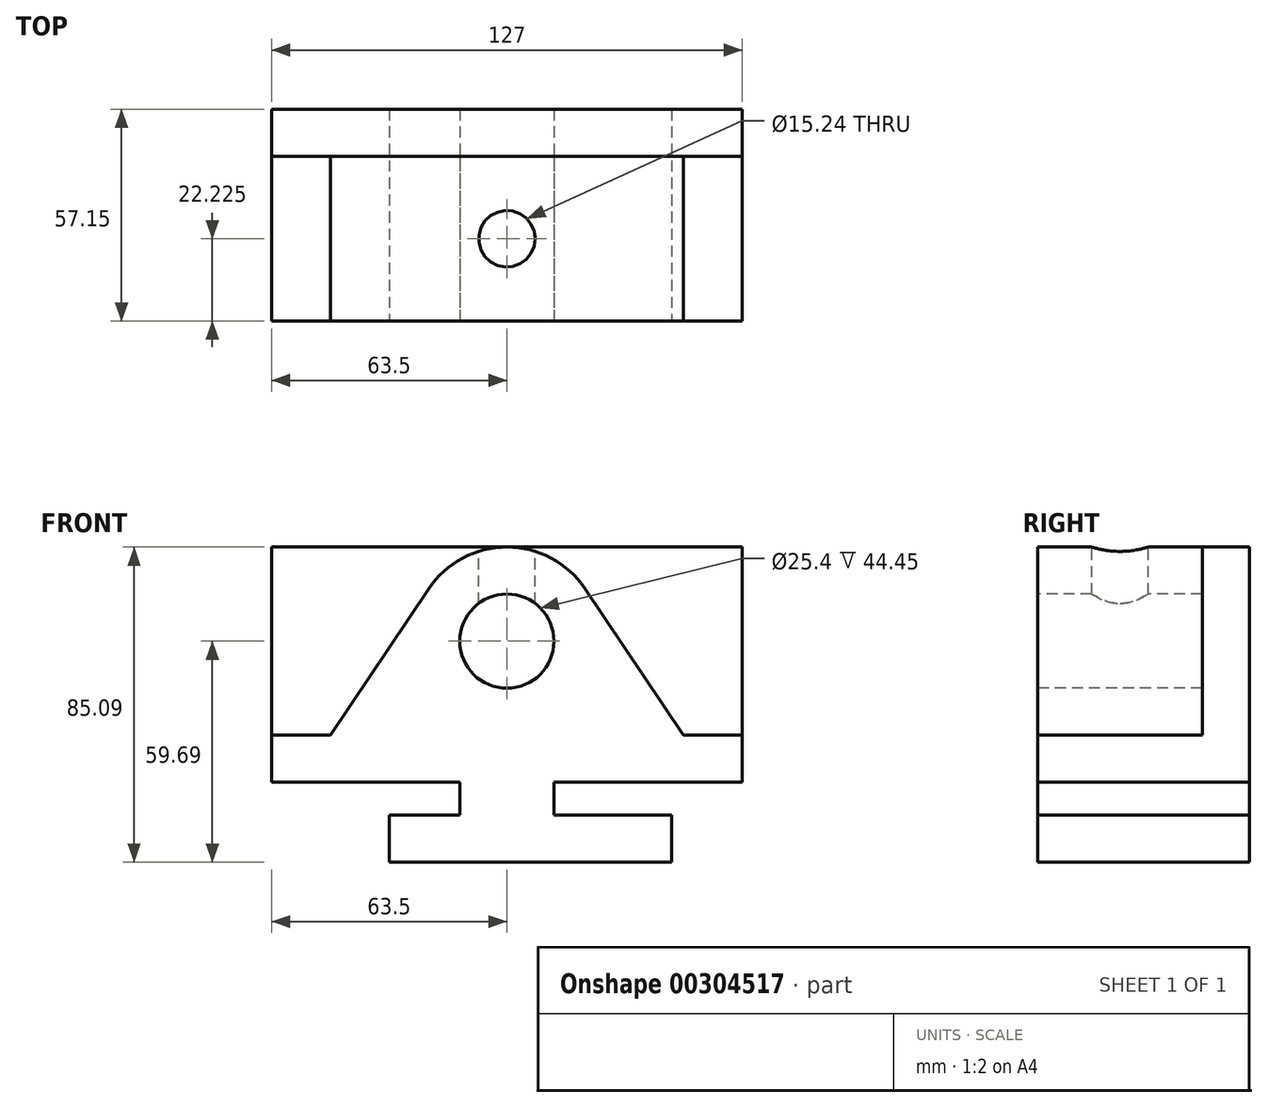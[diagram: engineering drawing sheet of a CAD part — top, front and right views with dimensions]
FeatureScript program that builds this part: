
annotation { "Feature Type Name" : "Feature", "Feature Type Description" : "" }
export const myFeature = defineFeature(function(context is Context, id is Id, definition is map)
    precondition{}
    {
        {
            var Q0;
            Q0=qCreatedBy(makeId("Right.planeOp"),FACE);
            var sketch = newSketch(context, id + "F0", { "sketchPlane" : qUnion([Q0])});
            skLineSegment(sketch, "E0", {"start": v(0, 0) * mm, "end": v(0, 85.1) * mm});
            skLineSegment(sketch, "E1", {"start": v(0, 85.1) * mm, "end": v(57.15, 85.1) * mm});
            skLineSegment(sketch, "E2", {"start": v(57.15, 85.1) * mm, "end": v(57.15, 0) * mm});
            skLineSegment(sketch, "E3", {"start": v(57.15, 0) * mm, "end": v(0, 0) * mm});
            skSolve(sketch);
        }
        {
            var Q0;
            Q0=makeQuery(id+"F0.imprint","IMPRINT",FACE,{"disambiguationData":[TD([[makeQuery(id+"F0.imprint","IMPRINT",EDGE,{"derivedFrom":sQuery(id+"F0.wireOp",EDGE,"E0")}),-1.0]])]});
            extrude(context, id + "F1", {"entities" : qUnion([Q0]), "endBound" : BoundingType.SYMMETRIC, "depth" : 127 * mm});
        }
        {
            var Q0;
            Q0=qCreatedBy(makeId("Front.planeOp"),FACE);
            var sketch = newSketch(context, id + "F2", { "sketchPlane" : qUnion([Q0])});
            skLineSegment(sketch, "E4", {"start": v(0, -6.5) * mm, "end": v(0, 68.36) * mm, "construction": true});
            skLineSegment(sketch, "E5", {"start": v(0, 0) * mm, "end": v(-31.75, 0) * mm});
            skLineSegment(sketch, "E6", {"start": v(-31.75, 0) * mm, "end": v(-31.75, 12.7) * mm});
            skLineSegment(sketch, "E7", {"start": v(-31.75, 12.7) * mm, "end": v(-12.7, 12.7) * mm});
            skLineSegment(sketch, "E8", {"start": v(-12.7, 12.7) * mm, "end": v(-12.7, 21.59) * mm});
            skLineSegment(sketch, "E9", {"start": v(-12.7, 21.6) * mm, "end": v(-63.5, 21.59) * mm});
            skLineSegment(sketch, "E10", {"start": v(-63.5, 21.59) * mm, "end": v(-63.5, 34.3) * mm});
            skLineSegment(sketch, "E11", {"start": v(-63.5, 34.3) * mm, "end": v(-47.63, 34.3) * mm});
            skLineSegment(sketch, "E12", {"start": v(-31.75, 0) * mm, "end": v(44.45, 0) * mm});
            skLineSegment(sketch, "E13", {"start": v(44.45, 0) * mm, "end": v(44.45, 12.7) * mm});
            skLineSegment(sketch, "E14", {"start": v(44.45, 12.7) * mm, "end": v(12.7, 12.7) * mm});
            skLineSegment(sketch, "E15", {"start": v(12.7, 12.7) * mm, "end": v(12.7, 21.59) * mm});
            skLineSegment(sketch, "E16", {"start": v(12.7, 21.6) * mm, "end": v(63.5, 21.6) * mm});
            skLineSegment(sketch, "E17", {"start": v(63.5, 21.6) * mm, "end": v(63.5, 34.3) * mm});
            skLineSegment(sketch, "E18", {"start": v(63.5, 34.3) * mm, "end": v(47.63, 34.3) * mm});
            skArc(sketch, "E19", {"start": v(21.1, 73.84) * mm, "mid": v(0, 85.1) * mm, "end": v(-21.1, 73.84) * mm});
            skLineSegment(sketch, "E20", {"start": v(-47.63, 34.3) * mm, "end": v(-21.1, 73.84) * mm});
            skLineSegment(sketch, "E21", {"start": v(21.1, 73.84) * mm, "end": v(47.63, 34.3) * mm});
            skCircle(sketch, "E22", {"center": v(0, 59.7) * mm, "radius": 12.7 * mm});
            skLineSegment(sketch, "E23", {"start": v(-63.5, 21.59) * mm, "end": v(-63.5, 0) * mm});
            skLineSegment(sketch, "E24", {"start": v(-63.5, 0) * mm, "end": v(-31.75, 0) * mm});
            skLineSegment(sketch, "E25", {"start": v(-63.5, 34.3) * mm, "end": v(-63.5, 85.1) * mm});
            skLineSegment(sketch, "E26", {"start": v(-63.5, 85.1) * mm, "end": v(63.5, 85.1) * mm});
            skLineSegment(sketch, "E27", {"start": v(63.5, 85.1) * mm, "end": v(63.5, 0) * mm});
            skLineSegment(sketch, "E28", {"start": v(0, 0) * mm, "end": v(63.5, 0) * mm});
            skSolve(sketch);
        }
        {
            var Q0;
            Q0=makeQuery(id+"F2.imprint","IMPRINT",FACE,{"disambiguationData":[TD([[makeQuery(id+"F2.imprint","IMPRINT",EDGE,{"derivedFrom":sQuery(id+"F2.wireOp",EDGE,"E11")}),1.0]])]});
            var Q1;
            {var subQ6=sQuery(id+"F2.wireOp",EDGE,"E18");Q1=makeQuery(id+"F2.imprint","IMPRINT",FACE,{"disambiguationData":[TD([[makeQuery(id+"F2.imprint","IMPRINT",EDGE,{"derivedFrom":subQ6}),-1.0]])]});}
            var Q2;
            Q2=makeQuery(id+"F2.imprint","IMPRINT",FACE,{"disambiguationData":[TD([[makeQuery(id+"F2.imprint","IMPRINT",EDGE,{"derivedFrom":sQuery(id+"F2.wireOp",EDGE,"E22")}),1.0]])]});
            extrude(context, id + "F3", {"entities" : qUnion([Q0, Q1, Q2]), "operationType" : NewBodyOperationType.REMOVE, "oppositeDirection" : true, "depth" : 44.45 * mm});
        }
        {
            var Q0;
            Q0=makeQuery(id+"F1.opExtrude","SWEPT_FACE",FACE,{"disambiguationData":[OSD([sQuery(id+"F0.wireOp",EDGE,"E1")])]});
            var sketch = newSketch(context, id + "F4", { "sketchPlane" : qUnion([Q0])});
            skCircle(sketch, "E29", {"center": v(0, 22.22) * mm, "radius": 7.62 * mm});
            skSolve(sketch);
        }
        {
            var Q0;
            Q0=makeQuery(id+"F4.imprint","IMPRINT",FACE,{"disambiguationData":[TD([[makeQuery(id+"F4.imprint","IMPRINT",EDGE,{"derivedFrom":sQuery(id+"F4.wireOp",EDGE,"E29")}),1.0]])]});
            extrude(context, id + "F5", {"entities" : qUnion([Q0]), "operationType" : NewBodyOperationType.REMOVE, "oppositeDirection" : true, "depth" : 25.4 * mm});
        }
        {
            var Q0;
            Q0=makeQuery(id+"F2.imprint","IMPRINT",FACE,{"disambiguationData":[TD([[makeQuery(id+"F2.imprint","IMPRINT",EDGE,{"derivedFrom":sQuery(id+"F2.wireOp",EDGE,"E6")}),1.0]])]});
            var Q1;
            {var subQ1=sQuery(id+"F2.wireOp",EDGE,"E13");Q1=makeQuery(id+"F2.imprint","IMPRINT",FACE,{"disambiguationData":[TD([[makeQuery(id+"F2.imprint","IMPRINT",EDGE,{"derivedFrom":subQ1}),-1.0]])]});}
            extrude(context, id + "F6", {"entities" : qUnion([Q0, Q1]), "operationType" : NewBodyOperationType.REMOVE, "endBound" : BoundingType.THROUGH_ALL, "oppositeDirection" : true, "depth" : 25.4 * mm});
        }
    });
